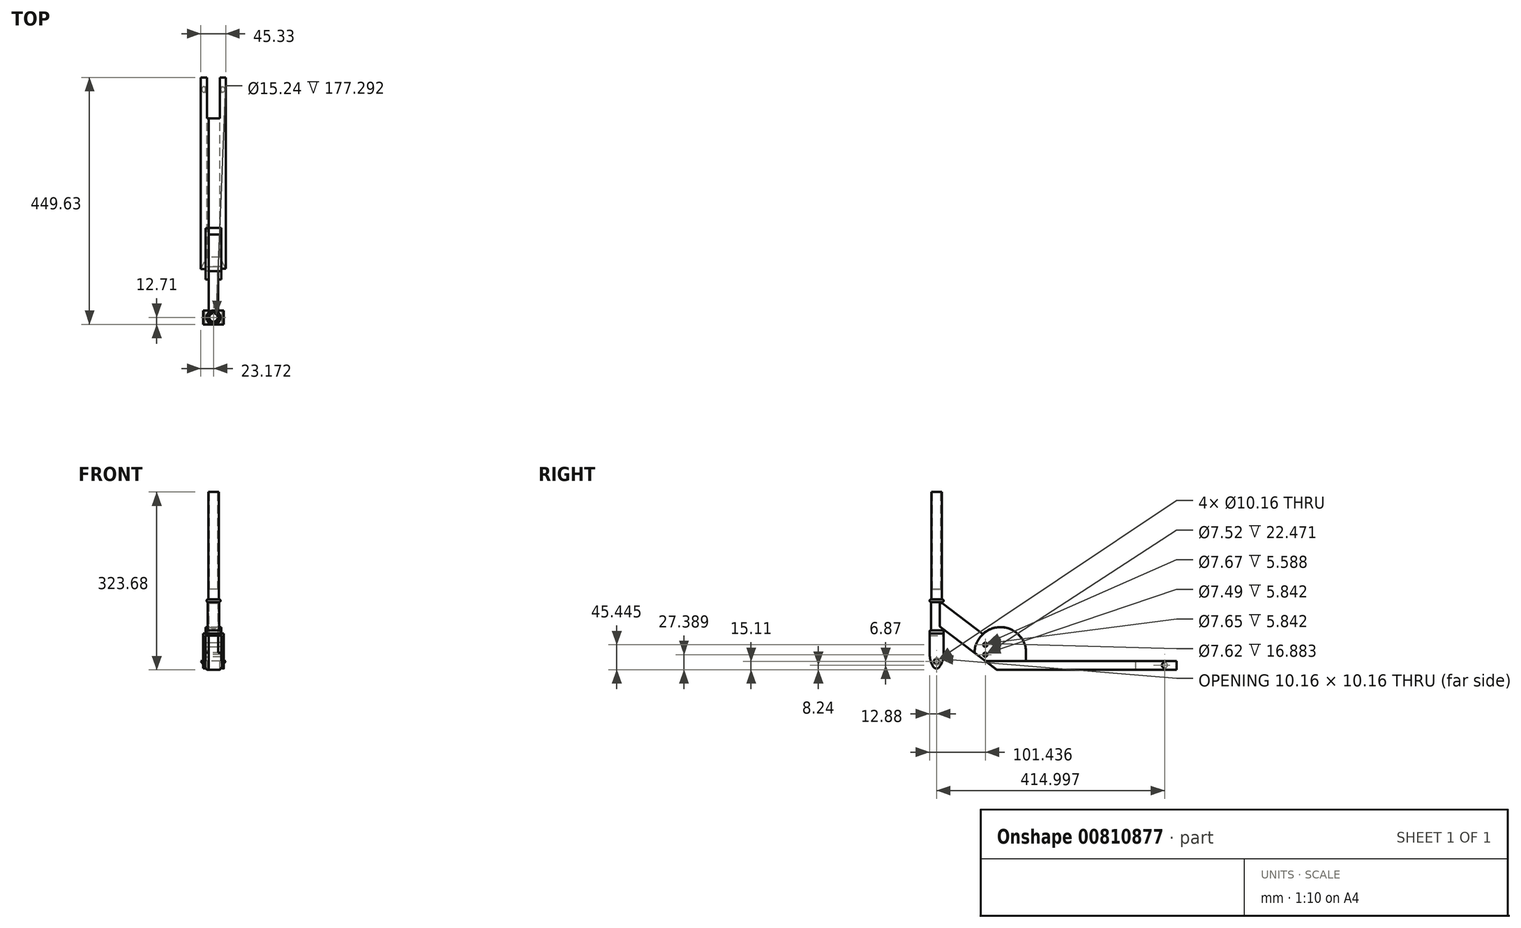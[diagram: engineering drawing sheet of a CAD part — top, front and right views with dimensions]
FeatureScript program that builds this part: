
annotation { "Feature Type Name" : "Feature", "Feature Type Description" : "" }
export const myFeature = defineFeature(function(context is Context, id is Id, definition is map)
    precondition{}
    {
        {
            var Q0;
            Q0=qCreatedBy(makeId("Front.planeOp"),FACE);
            var sketch = newSketch(context, id + "F0", { "sketchPlane" : qUnion([Q0])});
            skLineSegment(sketch, "E0", {"start": v(-49.91, 47.35) * mm, "end": v(-49.91, 0) * mm});
            skLineSegment(sketch, "E1", {"start": v(-19.3, 0) * mm, "end": v(-19.3, 47.35) * mm});
            skLineSegment(sketch, "E2", {"start": v(-19.3, 47.35) * mm, "end": v(-49.91, 47.35) * mm});
            skLineSegment(sketch, "E3", {"start": v(-49.91, 0) * mm, "end": v(-49.91, -18.03) * mm});
            skLineSegment(sketch, "E4", {"start": v(-19.3, 0) * mm, "end": v(-19.3, -18.03) * mm});
            skLineSegment(sketch, "E5", {"start": v(-49.91, -18.03) * mm, "end": v(-53.34, -18.03) * mm});
            skLineSegment(sketch, "E6", {"start": v(-53.34, -18.03) * mm, "end": v(-53.34, 50.76) * mm});
            skLineSegment(sketch, "E7", {"start": v(-53.34, 50.76) * mm, "end": v(-15.87, 50.76) * mm});
            skLineSegment(sketch, "E8", {"start": v(-15.87, 50.76) * mm, "end": v(-15.87, -18.03) * mm});
            skLineSegment(sketch, "E9", {"start": v(-15.87, -18.03) * mm, "end": v(-19.3, -18.03) * mm});
            skSolve(sketch);
        }
        {
            var Q0;
            Q0 = qSketchRegion(id + "F0", true);
            extrude(context, id + "F1", {"entities" : qUnion([Q0]), "depth" : 25.4 * mm, "offsetDistance" : 25.4 * mm});
        }
        {
            var Q0;
            Q0=makeQuery(id+"F1.opExtrude","SWEPT_FACE",FACE,{"disambiguationData":[OSD([sQuery(id+"F0.wireOp",EDGE,"E8")])]});
            var sketch = newSketch(context, id + "F2", { "sketchPlane" : qUnion([Q0])});
            skLineSegment(sketch, "E10", {"start": v(-25.4, 12.27) * mm, "end": v(-43.64, -15) * mm});
            skLineSegment(sketch, "E11", {"start": v(-43.64, -15) * mm, "end": v(-25.4, -23.49) * mm});
            skLineSegment(sketch, "E12", {"start": v(-25.4, -23.49) * mm, "end": v(-18.7, -18.03) * mm});
            skLineSegment(sketch, "E13", {"start": v(-6.75, -18.03) * mm, "end": v(4.55, -31.37) * mm});
            skLineSegment(sketch, "E14", {"start": v(4.55, -31.37) * mm, "end": v(10, -2.88) * mm});
            skLineSegment(sketch, "E15", {"start": v(10, -2.88) * mm, "end": v(0, 12.27) * mm});
            skArc(sketch, "E16", {"start": v(-25.4, 12.27) * mm, "mid": v(-23.37, 1.12) * mm, "end": v(-18.8, -9.24) * mm});
            skArc(sketch, "E17", {"start": v(-6.67, -8.64) * mm, "mid": v(-1.82, 1.33) * mm, "end": v(0, 12.27) * mm});
            skArc(sketch, "E18", {"start": v(-18.8, -9.24) * mm, "mid": v(-12.53, -12.91) * mm, "end": v(-6.67, -8.64) * mm});
            skLineSegment(sketch, "E19", {"start": v(-18.7, -18.03) * mm, "end": v(-6.75, -18.03) * mm});
            skSolve(sketch);
        }
        {
            var Q0;
            Q0 = qSketchRegion(id + "F2", true);
            extrude(context, id + "F3", {"entities" : qUnion([Q0]), "operationType" : NewBodyOperationType.REMOVE, "oppositeDirection" : true, "depth" : 124.2 * mm, "offsetDistance" : 25.4 * mm});
        }
        {
            var Q0;
            Q0=makeQuery(id+"F1.opExtrude","SWEPT_FACE",FACE,{"disambiguationData":[OSD([sQuery(id+"F0.wireOp",EDGE,"E8")])]});
            var sketch = newSketch(context, id + "F4", { "sketchPlane" : qUnion([Q0])});
            skCircle(sketch, "E20", {"center": v(-12.53, 0) * mm, "radius": 5.08 * mm});
            skPoint(sketch, "E20.centerSnap0", {"position": v(-12.53, -12.91) * mm});
            skSolve(sketch);
        }
        {
            var Q0;
            Q0 = qSketchRegion(id + "F4", true);
            extrude(context, id + "F5", {"entities" : qUnion([Q0]), "operationType" : NewBodyOperationType.REMOVE, "oppositeDirection" : true, "depth" : 61.2 * mm, "offsetDistance" : 25.4 * mm});
        }
        {
            var Q0;
            Q0=makeQuery(id+"F1.opExtrude","SWEPT_FACE",FACE,{"disambiguationData":[OSD([sQuery(id+"F0.wireOp",EDGE,"E7")])]});
            var sketch = newSketch(context, id + "F6", { "sketchPlane" : qUnion([Q0])});
            skCircle(sketch, "E21", {"center": v(-34.6, -12.7) * mm, "radius": 12.7 * mm});
            skPoint(sketch, "E21.centerSnap0", {"position": v(-53.34, -12.7) * mm});
            skPoint(sketch, "E21.centerSnap1", {"position": v(-34.6, -25.4) * mm});
            skSolve(sketch);
        }
        {
            var Q0;
            Q0 = qSketchRegion(id + "F6", true);
            extrude(context, id + "F7", {"entities" : qUnion([Q0]), "operationType" : NewBodyOperationType.ADD, "depth" : 6.1 * mm, "offsetDistance" : 25.4 * mm});
        }
        {
            var Q0;
            Q0=makeQuery(id+"F7.opExtrude","CAP_EDGE",EDGE,{"disambiguationData":[OSD([sQuery(id+"F6.wireOp",EDGE,"E21")])],"isStart":false});
            fillet(context, id + "F8", {"entities" : qUnion([Q0]), "radius" : 2.45 * mm, "tangentPropagation" : true, "allowEdgeOverflow" : false});
        }
        {
            var Q0;
            Q0=makeQuery(id+"F7.opExtrude","CAP_FACE",FACE,{"disambiguationData":[OSD([sQuery(id+"F6.wireOp",EDGE,"E21")])],"isStart":false});
            var sketch = newSketch(context, id + "F9", { "sketchPlane" : qUnion([Q0])});
            skCircle(sketch, "E22", {"center": v(-34.6, -12.7) * mm, "radius": 10.24 * mm});
            skSolve(sketch);
        }
        {
            var Q0;
            Q0 = qSketchRegion(id + "F9", true);
            extrude(context, id + "F10", {"entities" : qUnion([Q0]), "operationType" : NewBodyOperationType.ADD, "depth" : 51.3 * mm, "offsetDistance" : 25.4 * mm});
        }
        {
            var Q0;
            Q0=makeQuery(id+"F10.opExtrude","CAP_FACE",FACE,{"disambiguationData":[OSD([sQuery(id+"F9.wireOp",EDGE,"E22")])],"isStart":false});
            var sketch = newSketch(context, id + "F11", { "sketchPlane" : qUnion([Q0])});
            skCircle(sketch, "E23", {"center": v(-34.6, -12.7) * mm, "radius": 12.71 * mm});
            skSolve(sketch);
        }
        {
            var Q0;
            Q0 = qSketchRegion(id + "F11", true);
            extrude(context, id + "F12", {"entities" : qUnion([Q0]), "operationType" : NewBodyOperationType.ADD, "depth" : 4.83 * mm, "offsetDistance" : 25.4 * mm});
        }
        {
            var Q0;
            Q0=makeQuery(id+"F12.opExtrude","CAP_EDGE",EDGE,{"disambiguationData":[OSD([sQuery(id+"F11.wireOp",EDGE,"E23")])],"isStart":true});
            var Q1;
            Q1=makeQuery(id+"F12.opExtrude","CAP_EDGE",EDGE,{"disambiguationData":[OSD([sQuery(id+"F11.wireOp",EDGE,"E23")])],"isStart":false});
            fillet(context, id + "F13", {"entities" : qUnion([Q0, Q1]), "radius" : 2.33 * mm, "tangentPropagation" : true, "allowEdgeOverflow" : false});
        }
        {
            var Q0;
            Q0=makeQuery(id+"F12.opExtrude","CAP_FACE",FACE,{"disambiguationData":[OSD([sQuery(id+"F11.wireOp",EDGE,"E23")])],"isStart":false});
            var sketch = newSketch(context, id + "F14", { "sketchPlane" : qUnion([Q0])});
            skCircle(sketch, "E24", {"center": v(-34.6, -12.7) * mm, "radius": 9.57 * mm});
            skSolve(sketch);
        }
        {
            var Q0;
            Q0 = qSketchRegion(id + "F14", true);
            extrude(context, id + "F15", {"entities" : qUnion([Q0]), "operationType" : NewBodyOperationType.ADD, "depth" : 195.58 * mm, "offsetDistance" : 25.4 * mm});
        }
        {
            var Q0;
            Q0=makeQuery(id+"F15.opExtrude","CAP_FACE",FACE,{"disambiguationData":[OSD([sQuery(id+"F14.wireOp",EDGE,"E24")])],"isStart":false});
            var sketch = newSketch(context, id + "F16", { "sketchPlane" : qUnion([Q0])});
            skCircle(sketch, "E25", {"center": v(-34.6, -12.7) * mm, "radius": 7.62 * mm});
            skSolve(sketch);
        }
        {
            var Q0;
            Q0 = qSketchRegion(id + "F16", true);
            extrude(context, id + "F17", {"entities" : qUnion([Q0]), "operationType" : NewBodyOperationType.REMOVE, "oppositeDirection" : true, "depth" : 177.3 * mm, "offsetDistance" : 25.4 * mm});
        }
        {
            var Q0;
            Q0=qCreatedBy(makeId("Right.planeOp"),FACE);
            var sketch = newSketch(context, id + "F18", { "sketchPlane" : qUnion([Q0])});
            skLineSegment(sketch, "E26", {"start": v(-2.5, 105.87) * mm, "end": v(-6.9, 105.87) * mm});
            skLineSegment(sketch, "E27", {"start": v(-6.9, 105.87) * mm, "end": v(-6.9, 63.86) * mm});
            skLineSegment(sketch, "E28", {"start": v(-6.9, 63.86) * mm, "end": v(-2.2, 60.03) * mm});
            skLineSegment(sketch, "E29", {"start": v(-2.2, 60.03) * mm, "end": v(-2.5, 105.87) * mm});
            skSolve(sketch);
        }
        {
            var Q0;
            Q0 = qSketchRegion(id + "F18", true);
            extrude(context, id + "F19", {"entities" : qUnion([Q0]), "operationType" : NewBodyOperationType.REMOVE, "oppositeDirection" : true, "depth" : 64.77 * mm, "offsetDistance" : 25.4 * mm});
        }
        {
            var Q0;
            Q0=makeQuery(id+"F19.boolean.opBoolean","COPY",FACE,{"derivedFrom":makeQuery(id+"F19.opExtrude","SWEPT_FACE",FACE,{"disambiguationData":[OSD([sQuery(id+"F18.wireOp",EDGE,"E27")])]})});
            var sketch = newSketch(context, id + "F20", { "sketchPlane" : qUnion([Q0])});
            skLineSegment(sketch, "E30", {"start": v(31.56, 105.87) * mm, "end": v(33.5, 99.02) * mm});
            skLineSegment(sketch, "E31", {"start": v(33.5, 99.02) * mm, "end": v(39.73, 99.77) * mm});
            skLineSegment(sketch, "E32", {"start": v(39.73, 99.77) * mm, "end": v(38, 105.87) * mm});
            skLineSegment(sketch, "E33", {"start": v(38, 105.87) * mm, "end": v(31.56, 105.87) * mm});
            skSolve(sketch);
        }
        {
            var Q0;
            Q0 = qSketchRegion(id + "F20", true);
            extrude(context, id + "F21", {"entities" : qUnion([Q0]), "operationType" : NewBodyOperationType.REMOVE, "depth" : 25.4 * mm, "offsetDistance" : 25.4 * mm});
        }
        {
            var Q0;
            Q0=makeQuery(id+"F19.boolean.opBoolean","COPY",FACE,{"derivedFrom":makeQuery(id+"F19.opExtrude","SWEPT_FACE",FACE,{"disambiguationData":[OSD([sQuery(id+"F18.wireOp",EDGE,"E27")])]})});
            var Q1;
            Q1=makeQuery(id+"F19.boolean.opBoolean","COPY",FACE,{"derivedFrom":makeQuery(id+"F19.opExtrude","SWEPT_FACE",FACE,{"disambiguationData":[OSD([sQuery(id+"F18.wireOp",EDGE,"E28")])]})});
            extrude(context, id + "F22", {"entities" : qUnion([Q0, Q1]), "operationType" : NewBodyOperationType.ADD, "depth" : 4.32 * mm, "offsetDistance" : 25.4 * mm});
        }
        {
            var Q0;
            {var subQ0=sQuery(id+"F18.wireOp",EDGE,"E27");var subQ1=sQuery(id+"F9.wireOp",EDGE,"E22");Q0=makeQuery(id+"F22.opExtrude","SWEPT_FACE",FACE,{"disambiguationData":[OSD([subQ1,subQ0]),TDD([makeQuery(id+"F19.boolean.opBoolean","INTERSECT",EDGE,{"disambiguationData":[OD(0.0)],"derivedFrom":[makeQuery(id+"F10.opExtrude","SWEPT_FACE",FACE,{"disambiguationData":[OSD([subQ1])]}),makeQuery(id+"F19.opExtrude","SWEPT_FACE",FACE,{"disambiguationData":[OSD([subQ0])]})]})])]});}
            var sketch = newSketch(context, id + "F23", { "sketchPlane" : qUnion([Q0])});
            skLineSegment(sketch, "E34", {"start": v(6.9, 63.86) * mm, "end": v(-88.76, -8.69) * mm});
            skLineSegment(sketch, "E35", {"start": v(-88.76, -8.69) * mm, "end": v(-88.76, 36.88) * mm});
            skLineSegment(sketch, "E36", {"start": v(-88.76, 36.88) * mm, "end": v(2.59, 105.87) * mm});
            skLineSegment(sketch, "E37", {"start": v(2.59, 105.87) * mm, "end": v(6.9, 105.87) * mm});
            skLineSegment(sketch, "E38", {"start": v(6.9, 105.87) * mm, "end": v(6.9, 63.86) * mm});
            skSolve(sketch);
        }
        {
            var Q0;
            Q0 = qSketchRegion(id + "F23", true);
            var Q1;
            {var subQ0=sQuery(id+"F18.wireOp",EDGE,"E27");var subQ1=sQuery(id+"F9.wireOp",EDGE,"E22");Q1=makeQuery(id+"F22.opExtrude","SWEPT_FACE",FACE,{"disambiguationData":[OSD([subQ1,subQ0]),TDD([makeQuery(id+"F19.boolean.opBoolean","INTERSECT",EDGE,{"disambiguationData":[OD(1.0)],"derivedFrom":[makeQuery(id+"F10.opExtrude","SWEPT_FACE",FACE,{"disambiguationData":[OSD([subQ1])]}),makeQuery(id+"F19.opExtrude","SWEPT_FACE",FACE,{"disambiguationData":[OSD([subQ0])]})]})])]});}
            extrude(context, id + "F24", {"entities" : qUnion([Q0]), "operationType" : NewBodyOperationType.ADD, "endBound" : BoundingType.UP_TO_SURFACE, "oppositeDirection" : true, "depth" : 16.76 * mm, "endBoundEntityFace" : qUnion([Q1]), "offsetDistance" : 25.4 * mm});
        }
        {
            var Q0;
            {var subQ0=sQuery(id+"F18.wireOp",EDGE,"E27");var subQ1=sQuery(id+"F9.wireOp",EDGE,"E22");Q0=makeQuery(id+"FqCEreMiz1U5Pyt_1.boolean.opBoolean","MERGE",FACE,{"derivedFrom":[makeQuery(id+"F22.opExtrude","SWEPT_FACE",FACE,{"disambiguationData":[OSD([subQ1,subQ0]),TDD([makeQuery(id+"F19.boolean.opBoolean","INTERSECT",EDGE,{"disambiguationData":[OD(1.0)],"derivedFrom":[makeQuery(id+"F10.opExtrude","SWEPT_FACE",FACE,{"disambiguationData":[OSD([subQ1])]}),makeQuery(id+"F19.opExtrude","SWEPT_FACE",FACE,{"disambiguationData":[OSD([subQ0])]})]})])]}),makeQuery(id+"FqCEreMiz1U5Pyt_1.opExtrude","CAP_FACE",FACE,{"disambiguationData":[OSD([sQuery(id+"FuMQ6arrBUia2qR_1.wireOp",EDGE,"N2bbFlfP-p1yh-5LG0-l6nm-VKHmwcvaQ0Dd"),sQuery(id+"FuMQ6arrBUia2qR_1.wireOp",EDGE,"6zPFntCj-hYe6-yf68-lWXp-fEhB3Lck5cMx"),sQuery(id+"FuMQ6arrBUia2qR_1.wireOp",EDGE,"HAeMZwKg-vEOz-hymg-thl7-Cld8wh2kgTlV"),sQuery(id+"FuMQ6arrBUia2qR_1.wireOp",EDGE,"2npoZ4oi-h9Z7-1s7r-9WKr-3cLkbad8YobU"),sQuery(id+"FuMQ6arrBUia2qR_1.wireOp",EDGE,"Bm1DjaJD-gyY9-nHsA-yzby-exblkbxrOcUf")])],"isStart":true})]});}
            var sketch = newSketch(context, id + "F25", { "sketchPlane" : qUnion([Q0])});
            skCircle(sketch, "E39", {"center": v(76.03, 12.28) * mm, "radius": 3.8 * mm});
            skCircle(sketch, "E40", {"center": v(76.03, 30.34) * mm, "radius": 3.81 * mm});
            skSolve(sketch);
        }
        {
            var Q0;
            Q0 = qSketchRegion(id + "F25", true);
            extrude(context, id + "F26", {"entities" : qUnion([Q0]), "operationType" : NewBodyOperationType.REMOVE, "oppositeDirection" : true, "depth" : 25.4 * mm, "offsetDistance" : 25.4 * mm});
        }
        {
            var Q0;
            {var subQ0=sQuery(id+"F18.wireOp",EDGE,"E27");var subQ1=sQuery(id+"F9.wireOp",EDGE,"E22");Q0=makeQuery(id+"F24.boolean.opBoolean","MERGE",FACE,{"derivedFrom":[makeQuery(id+"F22.opExtrude","SWEPT_FACE",FACE,{"disambiguationData":[OSD([subQ1,subQ0]),TDD([makeQuery(id+"F19.boolean.opBoolean","INTERSECT",EDGE,{"disambiguationData":[OD(1.0)],"derivedFrom":[makeQuery(id+"F10.opExtrude","SWEPT_FACE",FACE,{"disambiguationData":[OSD([subQ1])]}),makeQuery(id+"F19.opExtrude","SWEPT_FACE",FACE,{"disambiguationData":[OSD([subQ0])]})]})])]}),makeQuery(id+"F24.opExtrude","CAP_FACE",FACE,{"disambiguationData":[OSD([subQ1,subQ0])],"isStart":false})]});}
            var sketch = newSketch(context, id + "F27", { "sketchPlane" : qUnion([Q0])});
            skLineSegment(sketch, "E41", {"start": v(88.76, -8.69) * mm, "end": v(97.17, -15.06) * mm});
            skLineSegment(sketch, "E42", {"start": v(97.17, -15.06) * mm, "end": v(424.22, -15.06) * mm});
            skLineSegment(sketch, "E43", {"start": v(150.09, 0.98) * mm, "end": v(424.22, 0.98) * mm});
            skLineSegment(sketch, "E44", {"start": v(88.76, -8.69) * mm, "end": v(88.76, 36.88) * mm});
            skLineSegment(sketch, "E45", {"start": v(424.22, 0.98) * mm, "end": v(424.22, -15.06) * mm});
            skArc(sketch, "E46", {"start": v(71.9, 49.62) * mm, "mid": v(60.61, 34.4) * mm, "end": v(56.25, 15.96) * mm});
            skArc(sketch, "E47", {"start": v(105.8, 62.45) * mm, "mid": v(87.54, 59.5) * mm, "end": v(71.9, 49.62) * mm});
            skArc(sketch, "E48", {"start": v(138.48, 46.55) * mm, "mid": v(123.77, 57.84) * mm, "end": v(105.8, 62.45) * mm});
            skArc(sketch, "E49", {"start": v(150.09, 13.01) * mm, "mid": v(147.78, 30.99) * mm, "end": v(138.48, 46.55) * mm});
            skLineSegment(sketch, "E50", {"start": v(150.09, 13.01) * mm, "end": v(150.09, 0.98) * mm});
            skPoint(sketch, "E51.orphan", {"position": v(134.47, 0.98) * mm});
            skLineSegment(sketch, "E52", {"start": v(56.25, 15.96) * mm, "end": v(97.17, -15.06) * mm});
            skCircle(sketch, "E53", {"center": v(76.03, 30.34) * mm, "radius": 3.84 * mm});
            skCircle(sketch, "E54", {"center": v(76.03, 12.28) * mm, "radius": 3.76 * mm});
            skSolve(sketch);
        }
        {
            var Q0;
            Q0 = qSketchRegion(id + "F27", true);
            extrude(context, id + "F28", {"entities" : qUnion([Q0]), "depth" : 13.72 * mm, "offsetDistance" : 25.4 * mm});
        }
        {
            var Q0;
            {var subQ0=sQuery(id+"F18.wireOp",EDGE,"E27");var subQ1=sQuery(id+"F9.wireOp",EDGE,"E22");Q0=makeQuery(id+"F24.boolean.opBoolean","MERGE",FACE,{"derivedFrom":[makeQuery(id+"F22.opExtrude","SWEPT_FACE",FACE,{"disambiguationData":[OSD([subQ1,subQ0]),TDD([makeQuery(id+"F19.boolean.opBoolean","INTERSECT",EDGE,{"disambiguationData":[OD(0.0)],"derivedFrom":[makeQuery(id+"F10.opExtrude","SWEPT_FACE",FACE,{"disambiguationData":[OSD([subQ1])]}),makeQuery(id+"F19.opExtrude","SWEPT_FACE",FACE,{"disambiguationData":[OSD([subQ0])]})]})])]}),makeQuery(id+"F24.opExtrude","CAP_FACE",FACE,{"disambiguationData":[OSD([sQuery(id+"F23.wireOp",EDGE,"E34"),sQuery(id+"F23.wireOp",EDGE,"E35"),sQuery(id+"F23.wireOp",EDGE,"E36"),sQuery(id+"F23.wireOp",EDGE,"E37"),sQuery(id+"F23.wireOp",EDGE,"E38")])],"isStart":true})]});}
            var sketch = newSketch(context, id + "F29", { "sketchPlane" : qUnion([Q0])});
            skArc(sketch, "E55", {"start": v(-56.6, 15.7) * mm, "mid": v(-101.24, 62.5) * mm, "end": v(-149.98, 20) * mm});
            skLineSegment(sketch, "E56", {"start": v(-149.98, 20) * mm, "end": v(-149.98, 1.02) * mm});
            skLineSegment(sketch, "E57", {"start": v(-149.98, 1.02) * mm, "end": v(-424.22, 1.02) * mm});
            skLineSegment(sketch, "E58", {"start": v(-424.22, 1.02) * mm, "end": v(-424.22, -15.1) * mm});
            skLineSegment(sketch, "E59", {"start": v(-424.22, -15.1) * mm, "end": v(-96.6, -15.1) * mm});
            skLineSegment(sketch, "E60", {"start": v(-96.6, -15.1) * mm, "end": v(-56.6, 15.7) * mm});
            skCircle(sketch, "E61", {"center": v(-76.03, 30.34) * mm, "radius": 3.83 * mm});
            skCircle(sketch, "E62", {"center": v(-76.03, 12.28) * mm, "radius": 3.75 * mm});
            skSolve(sketch);
        }
        {
            var Q0;
            Q0 = qSketchRegion(id + "F29", true);
            extrude(context, id + "F30", {"entities" : qUnion([Q0]), "depth" : 14.73 * mm, "offsetDistance" : 25.4 * mm});
        }
        {
            var Q0;
            Q0=makeQuery(id+"F28.opExtrude","CAP_FACE",FACE,{"disambiguationData":[OSD([sQuery(id+"F27.wireOp",EDGE,"E42"),sQuery(id+"F27.wireOp",EDGE,"E43"),sQuery(id+"F27.wireOp",EDGE,"E45"),sQuery(id+"F27.wireOp",EDGE,"E46"),sQuery(id+"F27.wireOp",EDGE,"E47"),sQuery(id+"F27.wireOp",EDGE,"E48"),sQuery(id+"F27.wireOp",EDGE,"E49"),sQuery(id+"F27.wireOp",EDGE,"E50"),sQuery(id+"F27.wireOp",EDGE,"E52"),sQuery(id+"F27.wireOp",EDGE,"E53"),sQuery(id+"F27.wireOp",EDGE,"E54")])],"isStart":true});
            var Q1;
            Q1=makeQuery(id+"F30.opExtrude","CAP_FACE",FACE,{"disambiguationData":[OSD([sQuery(id+"F29.wireOp",EDGE,"E55"),sQuery(id+"F29.wireOp",EDGE,"E56"),sQuery(id+"F29.wireOp",EDGE,"E57"),sQuery(id+"F29.wireOp",EDGE,"E58"),sQuery(id+"F29.wireOp",EDGE,"E59"),sQuery(id+"F29.wireOp",EDGE,"E60"),sQuery(id+"F29.wireOp",EDGE,"E61"),sQuery(id+"F29.wireOp",EDGE,"E62")])],"isStart":true});
            extrude(context, id + "F31", {"entities" : qUnion([Q0]), "operationType" : NewBodyOperationType.ADD, "endBound" : BoundingType.UP_TO_SURFACE, "depth" : 8.9 * mm, "endBoundEntityFace" : qUnion([Q1]), "offsetDistance" : 25.4 * mm});
        }
        {
            var Q0;
            Q0=makeQuery(id+"F30.opExtrude","CAP_FACE",FACE,{"disambiguationData":[OSD([sQuery(id+"F29.wireOp",EDGE,"E55"),sQuery(id+"F29.wireOp",EDGE,"E56"),sQuery(id+"F29.wireOp",EDGE,"E57"),sQuery(id+"F29.wireOp",EDGE,"E58"),sQuery(id+"F29.wireOp",EDGE,"E59"),sQuery(id+"F29.wireOp",EDGE,"E60"),sQuery(id+"F29.wireOp",EDGE,"E61"),sQuery(id+"F29.wireOp",EDGE,"E62")])],"isStart":false});
            var sketch = newSketch(context, id + "F32", { "sketchPlane" : qUnion([Q0])});
            skLineSegment(sketch, "E63", {"start": v(-149.98, 1.02) * mm, "end": v(-75.67, 1.02) * mm});
            skLineSegment(sketch, "E64", {"start": v(-75.67, 1.02) * mm, "end": v(-56.6, 15.7) * mm});
            skLineSegment(sketch, "E65", {"start": v(-56.6, 15.7) * mm, "end": v(-43.4, 37.34) * mm});
            skLineSegment(sketch, "E66", {"start": v(-43.4, 37.34) * mm, "end": v(-115.36, 92.8) * mm});
            skLineSegment(sketch, "E67", {"start": v(-115.36, 92.8) * mm, "end": v(-180.02, 61.42) * mm});
            skLineSegment(sketch, "E68", {"start": v(-180.02, 61.42) * mm, "end": v(-149.98, 1.02) * mm});
            skSolve(sketch);
        }
        {
            var Q0;
            Q0 = qSketchRegion(id + "F32", true);
            extrude(context, id + "F33", {"entities" : qUnion([Q0]), "operationType" : NewBodyOperationType.REMOVE, "oppositeDirection" : true, "depth" : 8.9 * mm, "offsetDistance" : 25.4 * mm});
        }
        {
            var Q0;
            Q0=makeQuery(id+"F28.opExtrude","CAP_FACE",FACE,{"disambiguationData":[OSD([sQuery(id+"F27.wireOp",EDGE,"E42"),sQuery(id+"F27.wireOp",EDGE,"E43"),sQuery(id+"F27.wireOp",EDGE,"E45"),sQuery(id+"F27.wireOp",EDGE,"E46"),sQuery(id+"F27.wireOp",EDGE,"E47"),sQuery(id+"F27.wireOp",EDGE,"E48"),sQuery(id+"F27.wireOp",EDGE,"E49"),sQuery(id+"F27.wireOp",EDGE,"E50"),sQuery(id+"F27.wireOp",EDGE,"E52"),sQuery(id+"F27.wireOp",EDGE,"E53"),sQuery(id+"F27.wireOp",EDGE,"E54")])],"isStart":false});
            var sketch = newSketch(context, id + "F34", { "sketchPlane" : qUnion([Q0])});
            skLineSegment(sketch, "E69", {"start": v(150.09, 0.98) * mm, "end": v(76.02, 0.98) * mm});
            skLineSegment(sketch, "E70", {"start": v(76.02, 0.98) * mm, "end": v(56.25, 15.96) * mm});
            skLineSegment(sketch, "E71", {"start": v(56.25, 15.96) * mm, "end": v(46.86, 46.1) * mm});
            skLineSegment(sketch, "E72", {"start": v(46.86, 46.1) * mm, "end": v(77.19, 75.92) * mm});
            skLineSegment(sketch, "E73", {"start": v(77.19, 75.92) * mm, "end": v(126.13, 64.4) * mm});
            skLineSegment(sketch, "E74", {"start": v(126.13, 64.4) * mm, "end": v(168.11, 38.41) * mm});
            skLineSegment(sketch, "E75", {"start": v(168.11, 38.41) * mm, "end": v(150.09, 0.98) * mm});
            skSolve(sketch);
        }
        {
            var Q0;
            Q0 = qSketchRegion(id + "F34", true);
            extrude(context, id + "F35", {"entities" : qUnion([Q0]), "operationType" : NewBodyOperationType.REMOVE, "oppositeDirection" : true, "depth" : 8.13 * mm, "offsetDistance" : 25.4 * mm});
        }
        {
            var Q0;
            {var subQ0=sQuery(id+"F27.wireOp",EDGE,"E43");Q0=makeQuery(id+"F35.boolean.opBoolean","MERGE",FACE,{"derivedFrom":[makeQuery(id+"F31.boolean.opBoolean","MERGE",FACE,{"derivedFrom":[makeQuery(id+"F28.opExtrude","SWEPT_FACE",FACE,{"disambiguationData":[OSD([subQ0])]}),makeQuery(id+"F31.opExtrude","SWEPT_FACE",FACE,{"disambiguationData":[OSD([subQ0])]})]}),makeQuery(id+"F35.opExtrude","SWEPT_FACE",FACE,{"disambiguationData":[OSD([sQuery(id+"F34.wireOp",EDGE,"E69")])]})]});}
            var sketch = newSketch(context, id + "F36", { "sketchPlane" : qUnion([Q0])});
            skLineSegment(sketch, "E76", {"start": v(-22.9, -45.27) * mm, "end": v(-22.9, 424.22) * mm});
            skLineSegment(sketch, "E77", {"start": v(-46.69, -45.27) * mm, "end": v(-46.69, 424.55) * mm});
            skLineSegment(sketch, "E78", {"start": v(-22.9, 349.82) * mm, "end": v(-46.69, 349.82) * mm});
            skLineSegment(sketch, "E79", {"start": v(-22.9, 424.22) * mm, "end": v(-46.69, 424.55) * mm});
            skSolve(sketch);
        }
        {
            var Q0;
            Q0 = qSketchRegion(id + "F36", true);
            extrude(context, id + "F37", {"entities" : qUnion([Q0]), "operationType" : NewBodyOperationType.REMOVE, "oppositeDirection" : true, "depth" : 25.4 * mm, "offsetDistance" : 25.4 * mm});
        }
        {
            var Q0;
            Q0=makeQuery(id+"F37.boolean.opBoolean","COPY",FACE,{"derivedFrom":makeQuery(id+"F37.opExtrude","CAP_FACE",FACE,{"disambiguationData":[OSD([sQuery(id+"F36.wireOp",EDGE,"E76"),sQuery(id+"F36.wireOp",EDGE,"E77"),sQuery(id+"F36.wireOp",EDGE,"E78"),sQuery(id+"F36.wireOp",EDGE,"E79")])],"isStart":true})});
            extrude(context, id + "F38", {"entities" : qUnion([Q0]), "operationType" : NewBodyOperationType.REMOVE, "oppositeDirection" : true, "depth" : 25.4 * mm, "offsetDistance" : 25.4 * mm});
        }
        {
            var Q0;
            Q0=makeQuery(id+"F28.opExtrude","CAP_FACE",FACE,{"disambiguationData":[OSD([sQuery(id+"F27.wireOp",EDGE,"E42"),sQuery(id+"F27.wireOp",EDGE,"E43"),sQuery(id+"F27.wireOp",EDGE,"E45"),sQuery(id+"F27.wireOp",EDGE,"E46"),sQuery(id+"F27.wireOp",EDGE,"E47"),sQuery(id+"F27.wireOp",EDGE,"E48"),sQuery(id+"F27.wireOp",EDGE,"E49"),sQuery(id+"F27.wireOp",EDGE,"E50"),sQuery(id+"F27.wireOp",EDGE,"E52"),sQuery(id+"F27.wireOp",EDGE,"E53"),sQuery(id+"F27.wireOp",EDGE,"E54")])],"isStart":false});
            var sketch = newSketch(context, id + "F39", { "sketchPlane" : qUnion([Q0])});
            skCircle(sketch, "E80", {"center": v(402.47, -6.87) * mm, "radius": 5.08 * mm});
            skSolve(sketch);
        }
        {
            var Q0;
            Q0 = qSketchRegion(id + "F39", true);
            extrude(context, id + "F40", {"entities" : qUnion([Q0]), "operationType" : NewBodyOperationType.REMOVE, "oppositeDirection" : true, "depth" : 70.36 * mm, "offsetDistance" : 25.4 * mm});
        }
        {
            var Q0;
            {var subQ0=sQuery(id+"F27.wireOp",EDGE,"E45");Q0=makeQuery(id+"F31.boolean.opBoolean","MERGE",FACE,{"derivedFrom":[makeQuery(id+"F28.opExtrude","SWEPT_FACE",FACE,{"disambiguationData":[OSD([subQ0])]}),makeQuery(id+"F31.opExtrude","SWEPT_FACE",FACE,{"disambiguationData":[OSD([subQ0])]})]});}
            var sketch = newSketch(context, id + "F41", { "sketchPlane" : qUnion([Q0])});
            skLineSegment(sketch, "E81", {"start": v(57.78, 1.02) * mm, "end": v(46.69, -15.1) * mm});
            skLineSegment(sketch, "E82", {"start": v(46.69, -15.1) * mm, "end": v(57.78, -15.1) * mm});
            skLineSegment(sketch, "E83", {"start": v(57.78, -15.1) * mm, "end": v(57.78, 1.02) * mm});
            skLineSegment(sketch, "E84", {"start": v(12.45, 0.98) * mm, "end": v(22.9, -15.06) * mm});
            skLineSegment(sketch, "E85", {"start": v(22.9, -15.06) * mm, "end": v(12.45, -15.06) * mm});
            skLineSegment(sketch, "E86", {"start": v(12.45, -15.06) * mm, "end": v(12.45, 0.98) * mm});
            skSolve(sketch);
        }
        {
            var Q0;
            Q0 = qSketchRegion(id + "F41", true);
            extrude(context, id + "F42", {"entities" : qUnion([Q0]), "operationType" : NewBodyOperationType.REMOVE, "oppositeDirection" : true, "depth" : 382.52 * mm, "offsetDistance" : 25.4 * mm});
        }
    });
